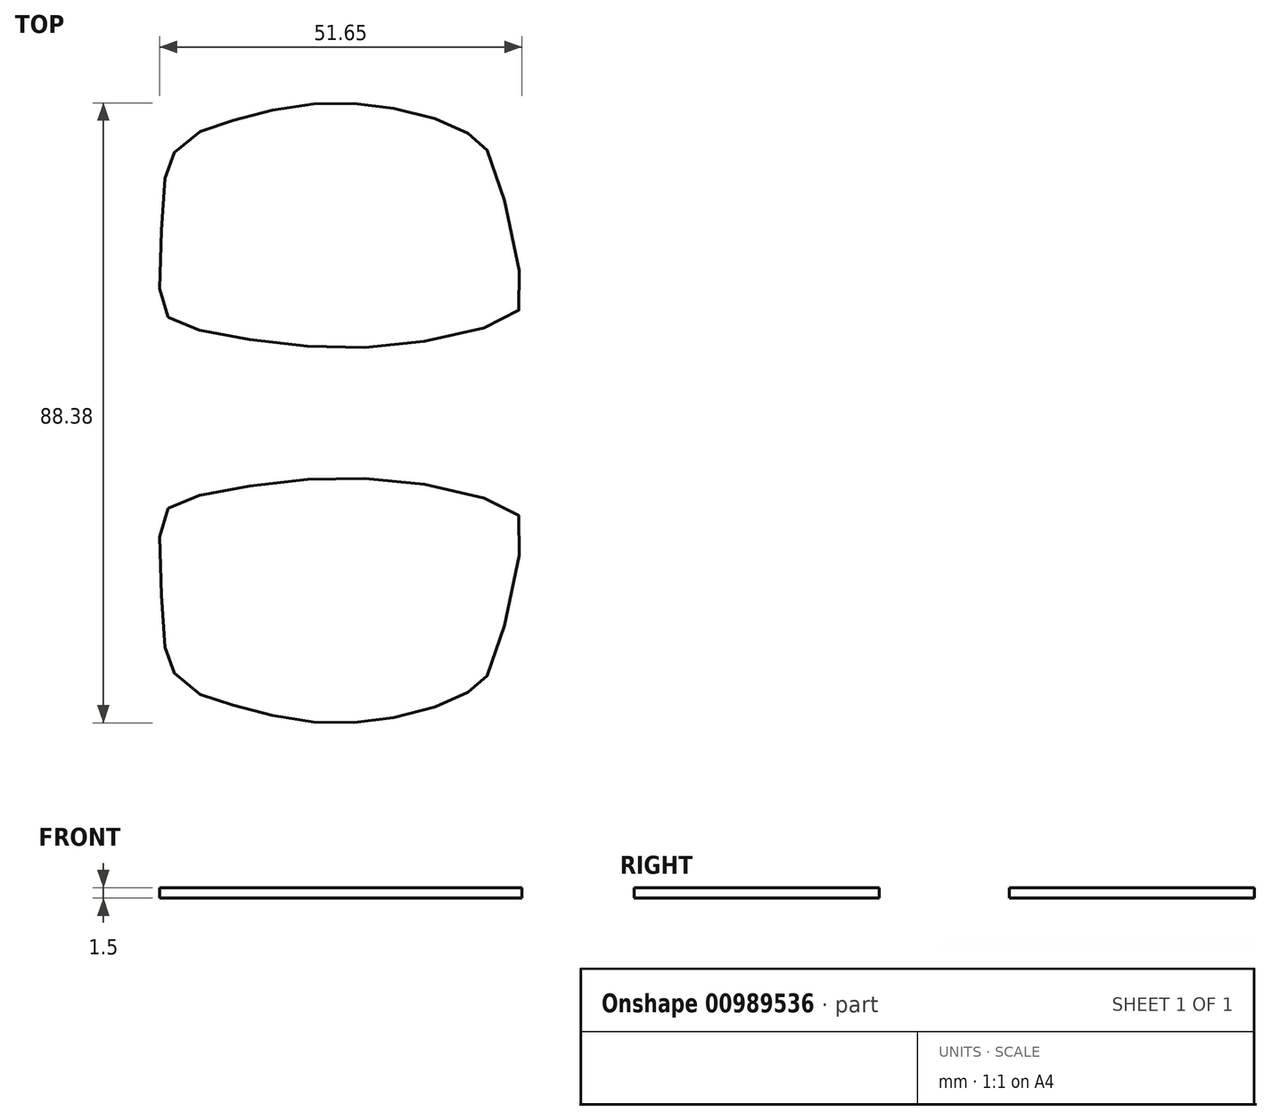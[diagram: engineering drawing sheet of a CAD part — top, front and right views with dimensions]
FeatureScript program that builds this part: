
annotation { "Feature Type Name" : "Feature", "Feature Type Description" : "" }
export const myFeature = defineFeature(function(context is Context, id is Id, definition is map)
    precondition{}
    {
        {
            var Q0;
            Q0=qCreatedBy(makeId("Top.planeOp"),FACE);
            var sketch = newSketch(context, id + "F0", { "sketchPlane" : qUnion([Q0])});
            skFitSpline(sketch, "E0", {"points": [v(-24.51, 12.88) * mm, v(-19.05, 14.93) * mm, v(-4.87, 16.98) * mm, v(10.85, 16.47) * mm, v(24.52, 12.7) * mm, v(25.88, 9.12) * mm, v(21.61, -9.67) * mm, v(19.4, -12.58) * mm, v(15.3, -14.8) * mm, v(7.26, -17.02) * mm, v(0, -17.7) * mm, v(-7.94, -17.02) * mm, v(-15.46, -15.14) * mm, v(-20.59, -13.26) * mm, v(-24.17, -9.84) * mm, v(-25.03, -5.91) * mm, v(-25.71, 9.12) * mm, v(-24.51, 12.88) * mm]});
            skLineSegment(sketch, "E1", {"start": v(-52.23, 26.49) * mm, "end": v(52.12, 26.49) * mm, "construction": true});
            skFitSpline(sketch, "E2.MirrorC", {"points": [v(-24.51, 40.1) * mm, v(-19.05, 38.05) * mm, v(-4.87, 36) * mm, v(10.85, 36.51) * mm, v(24.52, 40.27) * mm, v(25.88, 43.86) * mm, v(21.61, 62.65) * mm, v(19.4, 65.56) * mm, v(15.3, 67.78) * mm, v(7.26, 70) * mm, v(0, 70.68) * mm, v(-7.94, 70) * mm, v(-15.46, 68.12) * mm, v(-20.59, 66.24) * mm, v(-24.17, 62.82) * mm, v(-25.03, 58.9) * mm, v(-25.71, 43.86) * mm, v(-24.51, 40.1) * mm]});
            skSolve(sketch);
        }
        {
            var Q0;
            Q0 = qSketchRegion(id + "F0", true);
            var Q1;
            Q1=makeQuery(id+"F0.imprint","IMPRINT",FACE,{"disambiguationData":[TD([[makeQuery(id+"F0.imprint","IMPRINT",EDGE,{"derivedFrom":sQuery(id+"F0.wireOp",EDGE,"E0")}),-1.0]])]});
            extrude(context, id + "F1", {"entities" : qUnion([Q0, Q1]), "depth" : 1.5 * mm, "offsetDistance" : 25.4 * mm});
        }
    });
